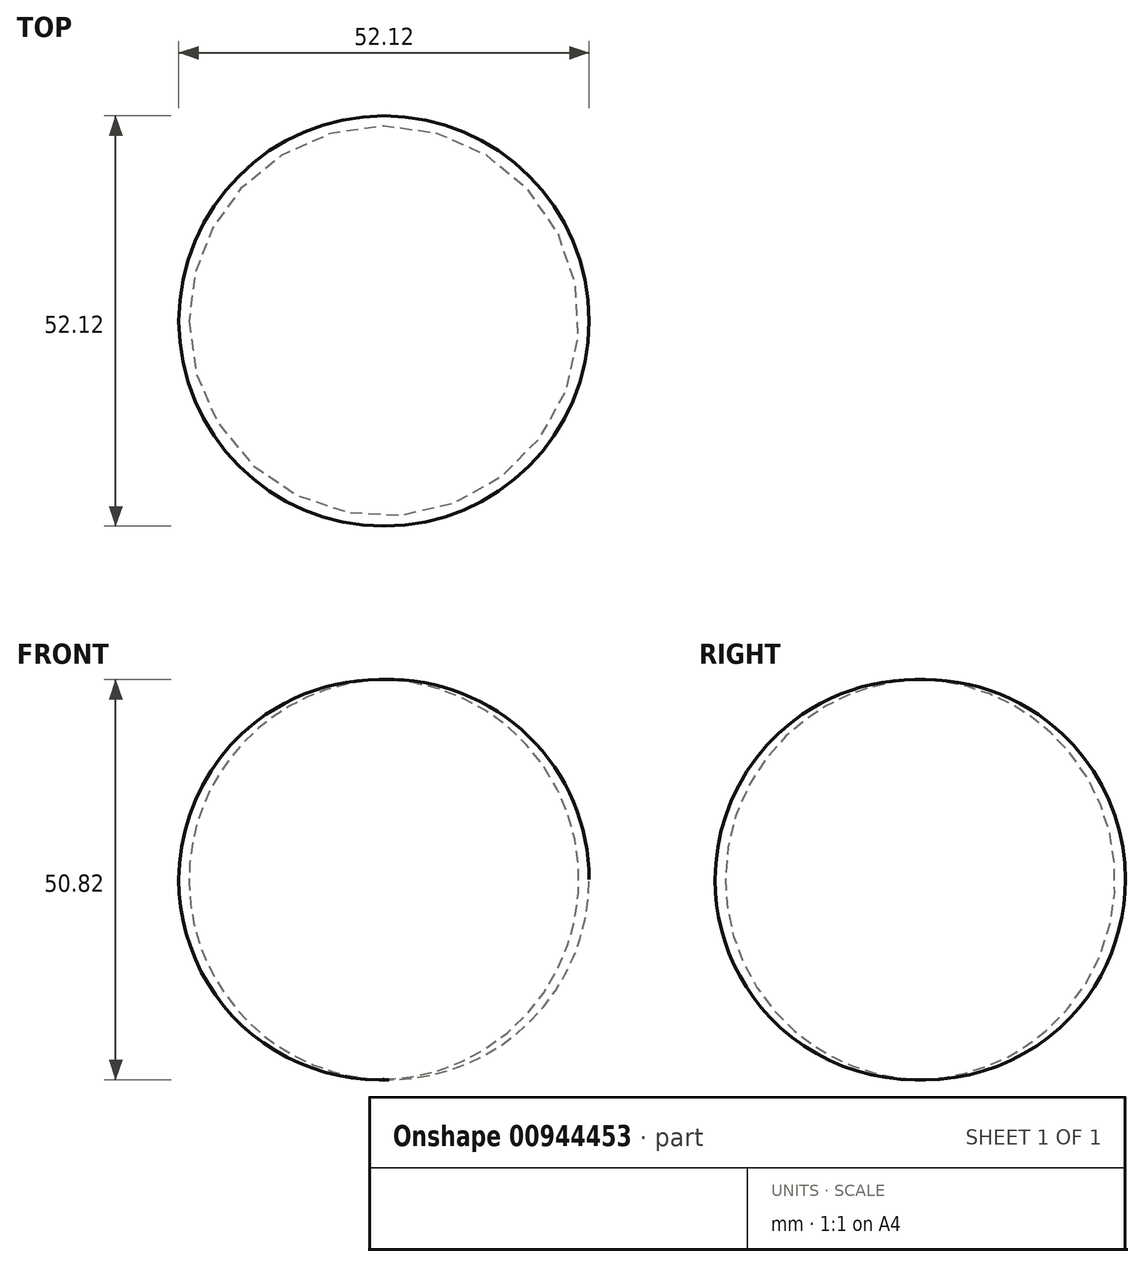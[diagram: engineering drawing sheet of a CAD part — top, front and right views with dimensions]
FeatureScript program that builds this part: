
annotation { "Feature Type Name" : "Feature", "Feature Type Description" : "" }
export const myFeature = defineFeature(function(context is Context, id is Id, definition is map)
    precondition{}
    {
        {
            var Q0;
            Q0=qCreatedBy(makeId("Front.planeOp"),FACE);
            var sketch = newSketch(context, id + "F0", { "sketchPlane" : qUnion([Q0])});
            skLineSegment(sketch, "E0", {"start": v(0, 50.8) * mm, "end": v(0, 0) * mm});
            skArc(sketch, "E1", {"start": v(0, 0) * mm, "mid": v(24.76, 25.4) * mm, "end": v(0, 50.8) * mm});
            skSolve(sketch);
        }
        {
            var Q0;
            Q0=makeQuery(id+"F0.imprint","IMPRINT",FACE,{"disambiguationData":[TD([[makeQuery(id+"F0.imprint","IMPRINT",EDGE,{"derivedFrom":sQuery(id+"F0.wireOp",EDGE,"E0")}),1.0]])]});
            var Q1;
            Q1=sQuery(id+"F0.wireOp",EDGE,"E0");
            revolve(context, id + "F1", {"surfaceOperationType" : NewSurfaceOperationType.NEW, "entities" : qUnion([Q0]), "axis" : qUnion([Q1]), "revolveType" : RevolveType.FULL});
        }
    });
